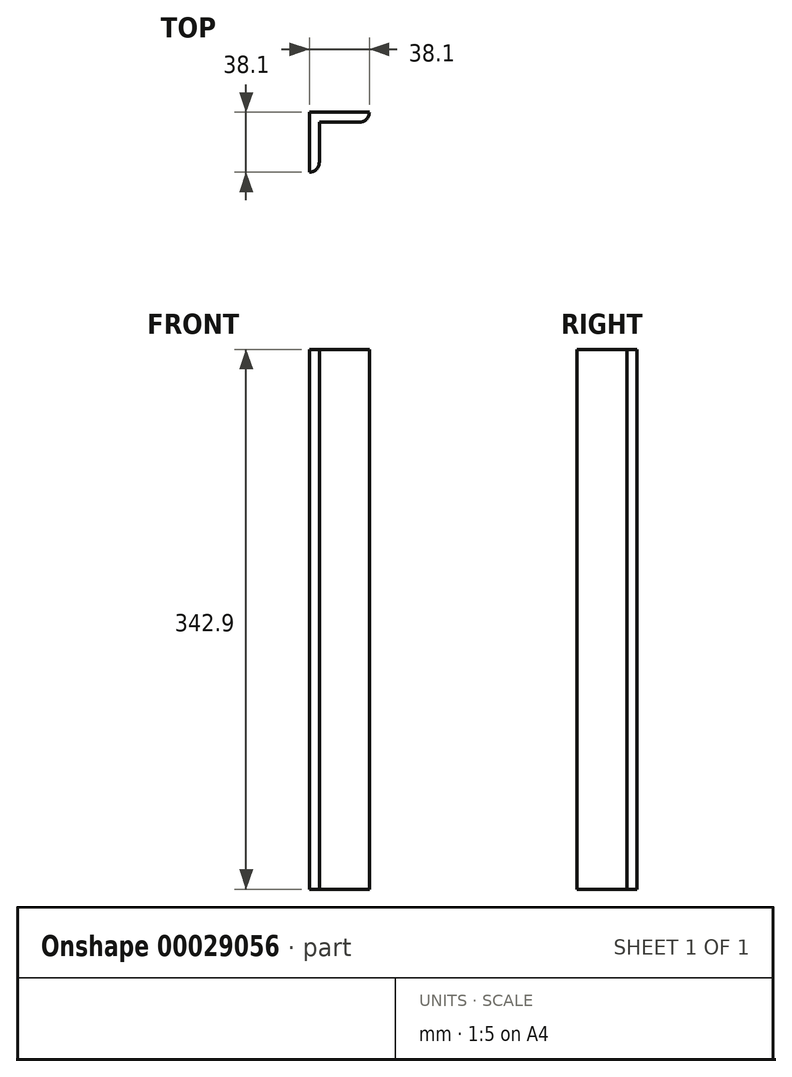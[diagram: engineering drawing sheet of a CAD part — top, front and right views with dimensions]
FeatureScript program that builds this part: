
annotation { "Feature Type Name" : "Feature", "Feature Type Description" : "" }
export const myFeature = defineFeature(function(context is Context, id is Id, definition is map)
    precondition{}
    {
        {
            var Q0;
            Q0=qCreatedBy(makeId("Top.planeOp"),FACE);
            var sketch = newSketch(context, id + "F0", { "sketchPlane" : qUnion([Q0])});
            skLineSegment(sketch, "E0.bottom", {"start": v(0, 0) * mm, "end": v(38.1, 0) * mm});
            skLineSegment(sketch, "E0.top", {"start": v(6.35, -6.35) * mm, "end": v(31.75, -6.35) * mm});
            skLineSegment(sketch, "E0.left", {"start": v(0, 0) * mm, "end": v(0, -6.35) * mm});
            skLineSegment(sketch, "E0.right", {"start": v(38.1, 0) * mm, "end": v(38.1, 0) * mm});
            skLineSegment(sketch, "E1.top", {"start": v(0, -38.1) * mm, "end": v(0, -38.1) * mm});
            skLineSegment(sketch, "E1.left", {"start": v(0, -6.35) * mm, "end": v(0, -38.1) * mm});
            skLineSegment(sketch, "E1.right", {"start": v(6.35, -6.35) * mm, "end": v(6.35, -31.75) * mm});
            skPoint(sketch, "E2.visualSharp", {"position": v(6.35, -38.1) * mm});
            skArc(sketch, "E2.filletArc", {"start": v(0, -38.1) * mm, "mid": v(4.5, -36.24) * mm, "end": v(6.35, -31.75) * mm});
            skPoint(sketch, "E3.visualSharp", {"position": v(38.1, -6.35) * mm});
            skArc(sketch, "E3.filletArc", {"start": v(31.75, -6.35) * mm, "mid": v(36.24, -4.5) * mm, "end": v(38.1, 0) * mm});
            skSolve(sketch);
        }
        {
            var Q0;
            Q0=makeQuery(id+"F0.imprint","IMPRINT",FACE,{"disambiguationData":[TD([[makeQuery(id+"F0.imprint","IMPRINT",EDGE,{"derivedFrom":sQuery(id+"F0.wireOp",EDGE,"E0.bottom")}),-1.0]])]});
            extrude(context, id + "F1", {"entities" : qUnion([Q0]), "depth" : 342.9 * mm});
        }
    });
